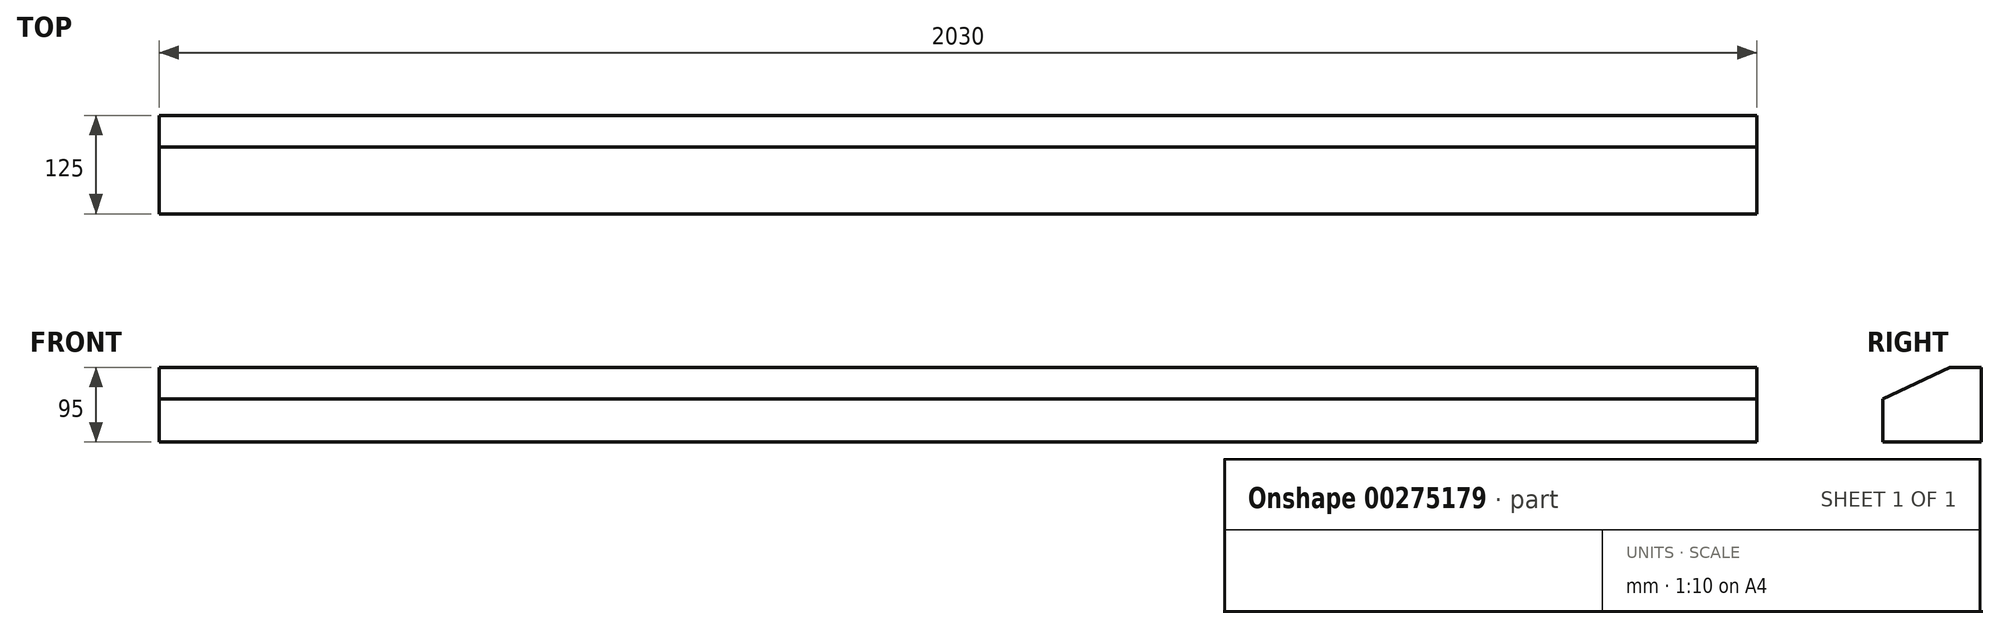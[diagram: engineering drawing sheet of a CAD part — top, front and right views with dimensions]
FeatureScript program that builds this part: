
annotation { "Feature Type Name" : "Feature", "Feature Type Description" : "" }
export const myFeature = defineFeature(function(context is Context, id is Id, definition is map)
    precondition{}
    {
        {
            var Q0;
            Q0=qCreatedBy(makeId("Front.planeOp"),FACE);
            var sketch = newSketch(context, id + "F0", { "sketchPlane" : qUnion([Q0])});
            skLineSegment(sketch, "E0.bottom", {"start": v(0, 0) * mm, "end": v(-2030, 0) * mm});
            skLineSegment(sketch, "E0.top", {"start": v(0, -95) * mm, "end": v(-2030, -95) * mm});
            skLineSegment(sketch, "E0.left", {"start": v(0, 0) * mm, "end": v(0, -95) * mm});
            skLineSegment(sketch, "E0.right", {"start": v(-2030, 0) * mm, "end": v(-2030, -95) * mm});
            skSolve(sketch);
        }
        {
            var Q0;
            Q0 = qSketchRegion(id + "F0", true);
            extrude(context, id + "F1", {"entities" : qUnion([Q0]), "depth" : 125 * mm});
        }
        {
            var Q0;
            Q0=makeQuery(id+"F1.opExtrude","CAP_EDGE",EDGE,{"disambiguationData":[OSD([sQuery(id+"F0.wireOp",EDGE,"E0.bottom")])],"isStart":false});
            chamfer(context, id + "F2", {"entities" : qUnion([Q0]), "chamferType" : ChamferType.TWO_OFFSETS, "width1" : 40 * mm, "oppositeDirection" : false, "width2" : 85 * mm, "tangentPropagation" : true});
        }
    });
